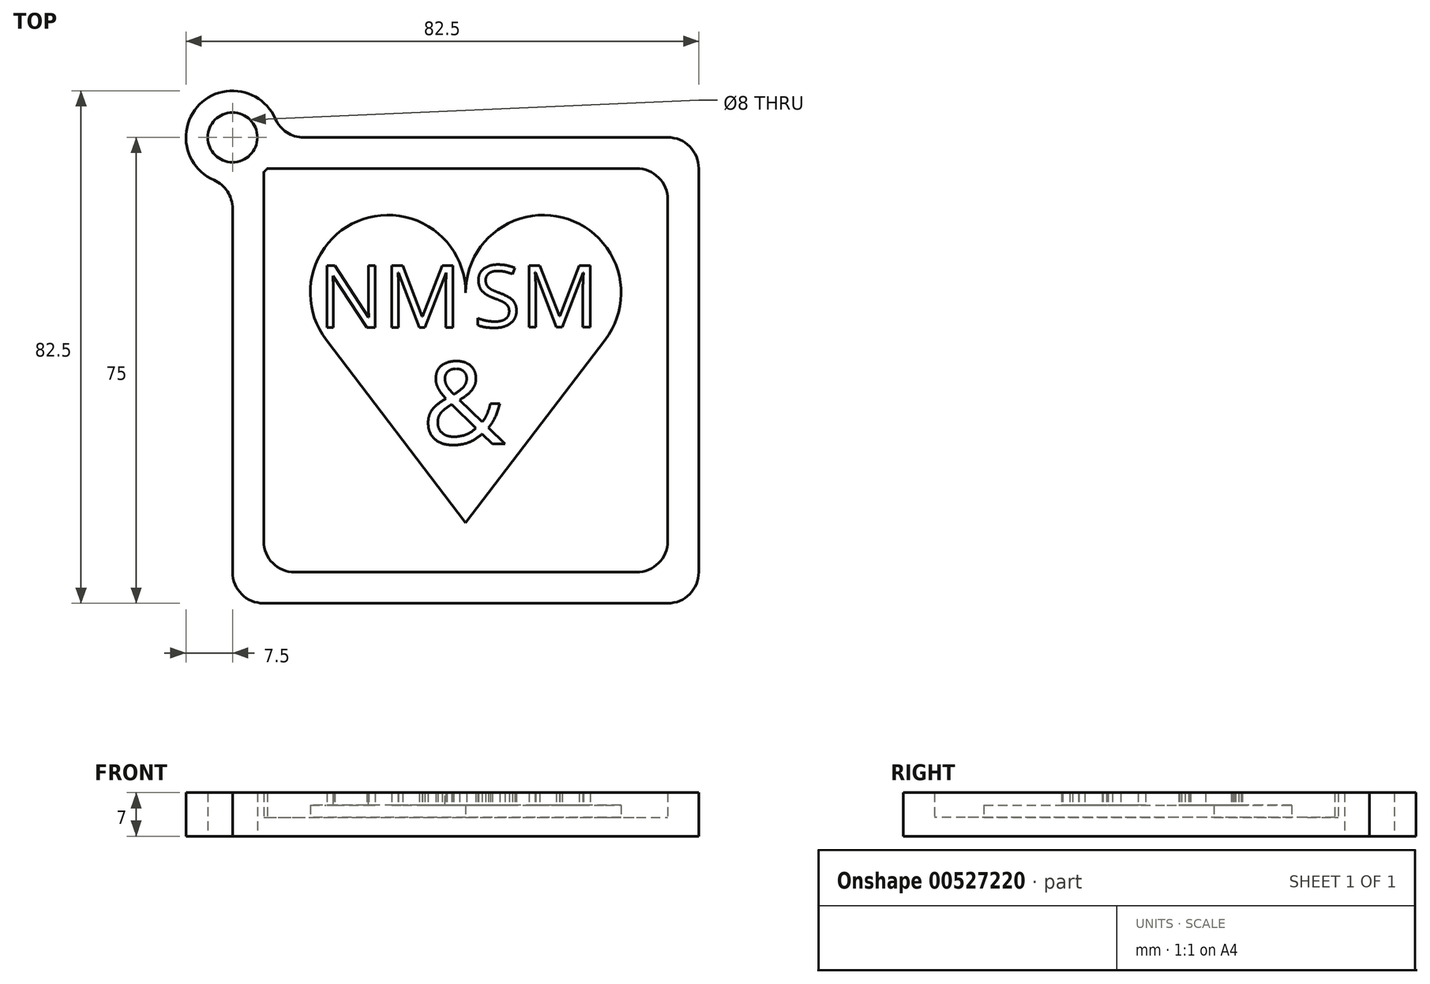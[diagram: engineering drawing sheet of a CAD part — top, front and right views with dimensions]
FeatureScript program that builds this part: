
annotation { "Feature Type Name" : "Feature", "Feature Type Description" : "" }
export const myFeature = defineFeature(function(context is Context, id is Id, definition is map)
    precondition{}
    {
        {
            var Q0;
            Q0=qCreatedBy(makeId("Top.planeOp"),FACE);
            var sketch = newSketch(context, id + "F0", { "sketchPlane" : qUnion([Q0])});
            skLineSegment(sketch, "E0.bottom", {"start": v(-37.5, 37.5) * mm, "end": v(37.5, 37.5) * mm});
            skLineSegment(sketch, "E0.top", {"start": v(-37.5, -37.5) * mm, "end": v(37.5, -37.5) * mm});
            skLineSegment(sketch, "E0.left", {"start": v(-37.5, 37.5) * mm, "end": v(-37.5, -37.5) * mm});
            skLineSegment(sketch, "E0.right", {"start": v(37.5, 37.5) * mm, "end": v(37.5, -37.5) * mm});
            skLineSegment(sketch, "E1.0", {"start": v(-32.5, 32.5) * mm, "end": v(32.5, 32.5) * mm});
            skLineSegment(sketch, "E1.1", {"start": v(-32.5, 32.5) * mm, "end": v(-32.5, -32.5) * mm});
            skLineSegment(sketch, "E1.2", {"start": v(-32.5, -32.5) * mm, "end": v(32.5, -32.5) * mm});
            skLineSegment(sketch, "E1.3", {"start": v(32.5, 32.5) * mm, "end": v(32.5, -32.5) * mm});
            skArc(sketch, "E2", {"start": v(0, 12.5) * mm, "mid": v(-16.5, 24.34) * mm, "end": v(-22.44, 4.93) * mm});
            skArc(sketch, "E3", {"start": v(22.44, 4.93) * mm, "mid": v(16.5, 24.34) * mm, "end": v(0, 12.5) * mm});
            skLineSegment(sketch, "E4", {"start": v(0, -24.54) * mm, "end": v(-22.44, 4.93) * mm});
            skLineSegment(sketch, "E5", {"start": v(0, -24.54) * mm, "end": v(22.44, 4.93) * mm});
            skCircle(sketch, "E6", {"center": v(-37.5, 37.5) * mm, "radius": 7.5 * mm});
            skCircle(sketch, "E7", {"center": v(-37.5, 37.5) * mm, "radius": 4 * mm});
            skSolve(sketch);
        }
        {
            var Q0;
            {var subQ1=sQuery(id+"F0.wireOp",EDGE,"E1.2");Q0=makeQuery(id+"F0.imprint","IMPRINT",FACE,{"disambiguationData":[TD([[makeQuery(id+"F0.imprint","IMPRINT",EDGE,{"derivedFrom":subQ1}),1.0]])]});}
            extrude(context, id + "F1", {"entities" : qUnion([Q0]), "depth" : 3 * mm, "offsetDistance" : 25 * mm});
        }
        {
            var Q0;
            Q0 = qSketchRegion(id + "F3", true);
            var Q1;
            {var subQ0=sQuery(id+"F0.wireOp",EDGE,"E6");var subQ1=sQuery(id+"F0.wireOp",EDGE,"E0.bottom");var subQ2=makeQuery(id+"F0.imprint","INTERSECT",VERTEX,{"derivedFrom":[subQ1,subQ0]});Q1=makeQuery(id+"F0.imprint","IMPRINT",FACE,{"disambiguationData":[TD([[makeQuery(id+"F0.imprint","IMPRINT",EDGE,{"disambiguationData":[TD([[subQ2,1.0]])],"derivedFrom":subQ1}),1.0]])]});}
            var Q2;
            {var subQ0=sQuery(id+"F0.wireOp",EDGE,"E6");var subQ1=sQuery(id+"F0.wireOp",EDGE,"E0.left");var subQ2=makeQuery(id+"F0.imprint","INTERSECT",VERTEX,{"derivedFrom":[subQ1,subQ0]});Q2=makeQuery(id+"F0.imprint","IMPRINT",FACE,{"disambiguationData":[TD([[makeQuery(id+"F0.imprint","IMPRINT",EDGE,{"disambiguationData":[TD([[subQ2,1.0]])],"derivedFrom":subQ1}),1.0]])]});}
            var Q3;
            {var subQ0=sQuery(id+"F0.wireOp",EDGE,"E6");var subQ1=sQuery(id+"F0.wireOp",EDGE,"E0.bottom");var subQ2=makeQuery(id+"F0.imprint","INTERSECT",VERTEX,{"derivedFrom":[subQ1,subQ0]});Q3=makeQuery(id+"F0.imprint","IMPRINT",FACE,{"disambiguationData":[TD([[makeQuery(id+"F0.imprint","IMPRINT",EDGE,{"disambiguationData":[TD([[subQ2,1.0]])],"derivedFrom":subQ1}),-1.0]])]});}
            var Q4;
            {var subQ1=sQuery(id+"F0.wireOp",EDGE,"E0.top");Q4=makeQuery(id+"F0.imprint","IMPRINT",FACE,{"disambiguationData":[TD([[makeQuery(id+"F0.imprint","IMPRINT",EDGE,{"derivedFrom":subQ1}),1.0]])]});}
            var Q5;
            {var subQ1=sQuery(id+"F0.wireOp",EDGE,"E1.0");var subQ3=sQuery(id+"F0.wireOp",EDGE,"E6");var subQ4=makeQuery(id+"F0.imprint","INTERSECT",VERTEX,{"derivedFrom":[subQ1,subQ3]});Q5=makeQuery(id+"F0.imprint","IMPRINT",FACE,{"disambiguationData":[TD([[makeQuery(id+"F0.imprint","IMPRINT",EDGE,{"disambiguationData":[TD([[subQ4,1.0]])],"derivedFrom":subQ3}),1.0]])]});}
            var Q6;
            Q6=makeQuery(id+"F0.imprint","IMPRINT",FACE,{"disambiguationData":[TD([[makeQuery(id+"F0.imprint","IMPRINT",EDGE,{"derivedFrom":sQuery(id+"F0.wireOp",EDGE,"E2")}),1.0]])]});
            extrude(context, id + "F2", {"entities" : qUnion([Q0, Q1, Q2, Q3, Q4, Q5, Q6]), "operationType" : NewBodyOperationType.ADD, "depth" : 5 * mm, "offsetDistance" : 25 * mm});
        }
        {
            var Q0;
            Q0=makeQuery(id+"F2.opExtrude","CAP_FACE",FACE,{"disambiguationData":[OSD([sQuery(id+"F0.wireOp",EDGE,"E2"),sQuery(id+"F0.wireOp",EDGE,"E3"),sQuery(id+"F0.wireOp",EDGE,"E4"),sQuery(id+"F0.wireOp",EDGE,"E5")])],"isStart":false});
            var sketch = newSketch(context, id + "F3", { "sketchPlane" : qUnion([Q0])});
            skText(sketch, "E8", { "text": "NM", "fontName": "OpenSans-Regular.ttf"});
            skText(sketch, "E9", { "text": "SM", "fontName": "OpenSans-Regular.ttf"});
            skText(sketch, "E10", { "text": "&", "fontName": "OpenSans-Regular.ttf"});
            const initialGuessF3  = {"E8": [-0.0237, 0.00692, 1, 0, 0.01], "E9": [0.00121, 0.00697, 1, 0, 0.01], "E10": [-0.00705, -0.01185, 1, 0, 0.01324]};
            skSetInitialGuess(sketch, initialGuessF3);
            skSolve(sketch);
        }
        {
            var Q0;
            Q0 = qSketchRegion(id + "F3", true);
            extrude(context, id + "F4", {"entities" : qUnion([Q0]), "operationType" : NewBodyOperationType.ADD, "depth" : 2 * mm, "offsetDistance" : 25 * mm});
        }
        {
            var Q0;
            Q0=makeQuery(id+"F2.opExtrude","CAP_FACE",FACE,{"disambiguationData":[OSD([sQuery(id+"F0.wireOp",EDGE,"E0.bottom"),sQuery(id+"F0.wireOp",EDGE,"E0.top"),sQuery(id+"F0.wireOp",EDGE,"E0.left"),sQuery(id+"F0.wireOp",EDGE,"E0.right"),sQuery(id+"F0.wireOp",EDGE,"E1.0"),sQuery(id+"F0.wireOp",EDGE,"E1.1"),sQuery(id+"F0.wireOp",EDGE,"E1.2"),sQuery(id+"F0.wireOp",EDGE,"E1.3"),sQuery(id+"F0.wireOp",EDGE,"E6"),sQuery(id+"F0.wireOp",EDGE,"E7")])],"isStart":false});
            extrude(context, id + "F5", {"entities" : qUnion([Q0]), "operationType" : NewBodyOperationType.ADD, "depth" : 2 * mm, "offsetDistance" : 25 * mm});
        }
        {
            var Q0;
            {var subQ0=sQuery(id+"F0.wireOp",EDGE,"E0.left");var subQ1=sQuery(id+"F0.wireOp",EDGE,"E0.top");Q0=makeQuery(id+"F5.boolean.opBoolean","MERGE",EDGE,{"derivedFrom":[makeQuery(id+"F2.opExtrude","SWEPT_EDGE",EDGE,{"disambiguationData":[OSD([subQ1,subQ0])]}),makeQuery(id+"F5.opExtrude","SWEPT_EDGE",EDGE,{"disambiguationData":[OSD([subQ1,subQ0])]})]});}
            var Q1;
            {var subQ0=sQuery(id+"F0.wireOp",EDGE,"E0.right");var subQ1=sQuery(id+"F0.wireOp",EDGE,"E0.top");Q1=makeQuery(id+"F5.boolean.opBoolean","MERGE",EDGE,{"derivedFrom":[makeQuery(id+"F2.opExtrude","SWEPT_EDGE",EDGE,{"disambiguationData":[OSD([subQ1,subQ0])]}),makeQuery(id+"F5.opExtrude","SWEPT_EDGE",EDGE,{"disambiguationData":[OSD([subQ1,subQ0])]})]});}
            var Q2;
            {var subQ0=sQuery(id+"F0.wireOp",EDGE,"E0.right");var subQ1=sQuery(id+"F0.wireOp",EDGE,"E0.bottom");Q2=makeQuery(id+"F5.boolean.opBoolean","MERGE",EDGE,{"derivedFrom":[makeQuery(id+"F2.opExtrude","SWEPT_EDGE",EDGE,{"disambiguationData":[OSD([subQ1,subQ0])]}),makeQuery(id+"F5.opExtrude","SWEPT_EDGE",EDGE,{"disambiguationData":[OSD([subQ1,subQ0])]})]});}
            var Q3;
            {var subQ0=sQuery(id+"F0.wireOp",EDGE,"E6");var subQ1=sQuery(id+"F0.wireOp",EDGE,"E0.bottom");Q3=makeQuery(id+"F5.boolean.opBoolean","MERGE",EDGE,{"derivedFrom":[makeQuery(id+"F2.opExtrude","SWEPT_EDGE",EDGE,{"disambiguationData":[OSD([subQ1,subQ0])]}),makeQuery(id+"F5.opExtrude","SWEPT_EDGE",EDGE,{"disambiguationData":[OSD([subQ1,subQ0])]})]});}
            var Q4;
            {var subQ0=sQuery(id+"F0.wireOp",EDGE,"E6");var subQ1=sQuery(id+"F0.wireOp",EDGE,"E0.left");Q4=makeQuery(id+"F5.boolean.opBoolean","MERGE",EDGE,{"derivedFrom":[makeQuery(id+"F2.opExtrude","SWEPT_EDGE",EDGE,{"disambiguationData":[OSD([subQ1,subQ0])]}),makeQuery(id+"F5.opExtrude","SWEPT_EDGE",EDGE,{"disambiguationData":[OSD([subQ1,subQ0])]})]});}
            var Q5;
            {var subQ0=sQuery(id+"F0.wireOp",EDGE,"E1.3");var subQ1=sQuery(id+"F0.wireOp",EDGE,"E1.0");Q5=makeQuery(id+"F5.boolean.opBoolean","MERGE",EDGE,{"derivedFrom":[makeQuery(id+"F2.opExtrude","SWEPT_EDGE",EDGE,{"disambiguationData":[OSD([subQ1,subQ0])]}),makeQuery(id+"F5.opExtrude","SWEPT_EDGE",EDGE,{"disambiguationData":[OSD([subQ1,subQ0])]})]});}
            var Q6;
            {var subQ0=sQuery(id+"F0.wireOp",EDGE,"E1.3");var subQ1=sQuery(id+"F0.wireOp",EDGE,"E1.2");Q6=makeQuery(id+"F5.boolean.opBoolean","MERGE",EDGE,{"derivedFrom":[makeQuery(id+"F2.opExtrude","SWEPT_EDGE",EDGE,{"disambiguationData":[OSD([subQ1,subQ0])]}),makeQuery(id+"F5.opExtrude","SWEPT_EDGE",EDGE,{"disambiguationData":[OSD([subQ1,subQ0])]})]});}
            var Q7;
            {var subQ0=sQuery(id+"F0.wireOp",EDGE,"E1.2");var subQ1=sQuery(id+"F0.wireOp",EDGE,"E1.1");Q7=makeQuery(id+"F5.boolean.opBoolean","MERGE",EDGE,{"derivedFrom":[makeQuery(id+"F2.opExtrude","SWEPT_EDGE",EDGE,{"disambiguationData":[OSD([subQ1,subQ0])]}),makeQuery(id+"F5.opExtrude","SWEPT_EDGE",EDGE,{"disambiguationData":[OSD([subQ1,subQ0])]})]});}
            fillet(context, id + "F6", {"entities" : qUnion([Q0, Q1, Q2, Q3, Q4, Q5, Q6, Q7]), "radius" : 5 * mm, "tangentPropagation" : true, "allowEdgeOverflow" : false});
        }
    });
